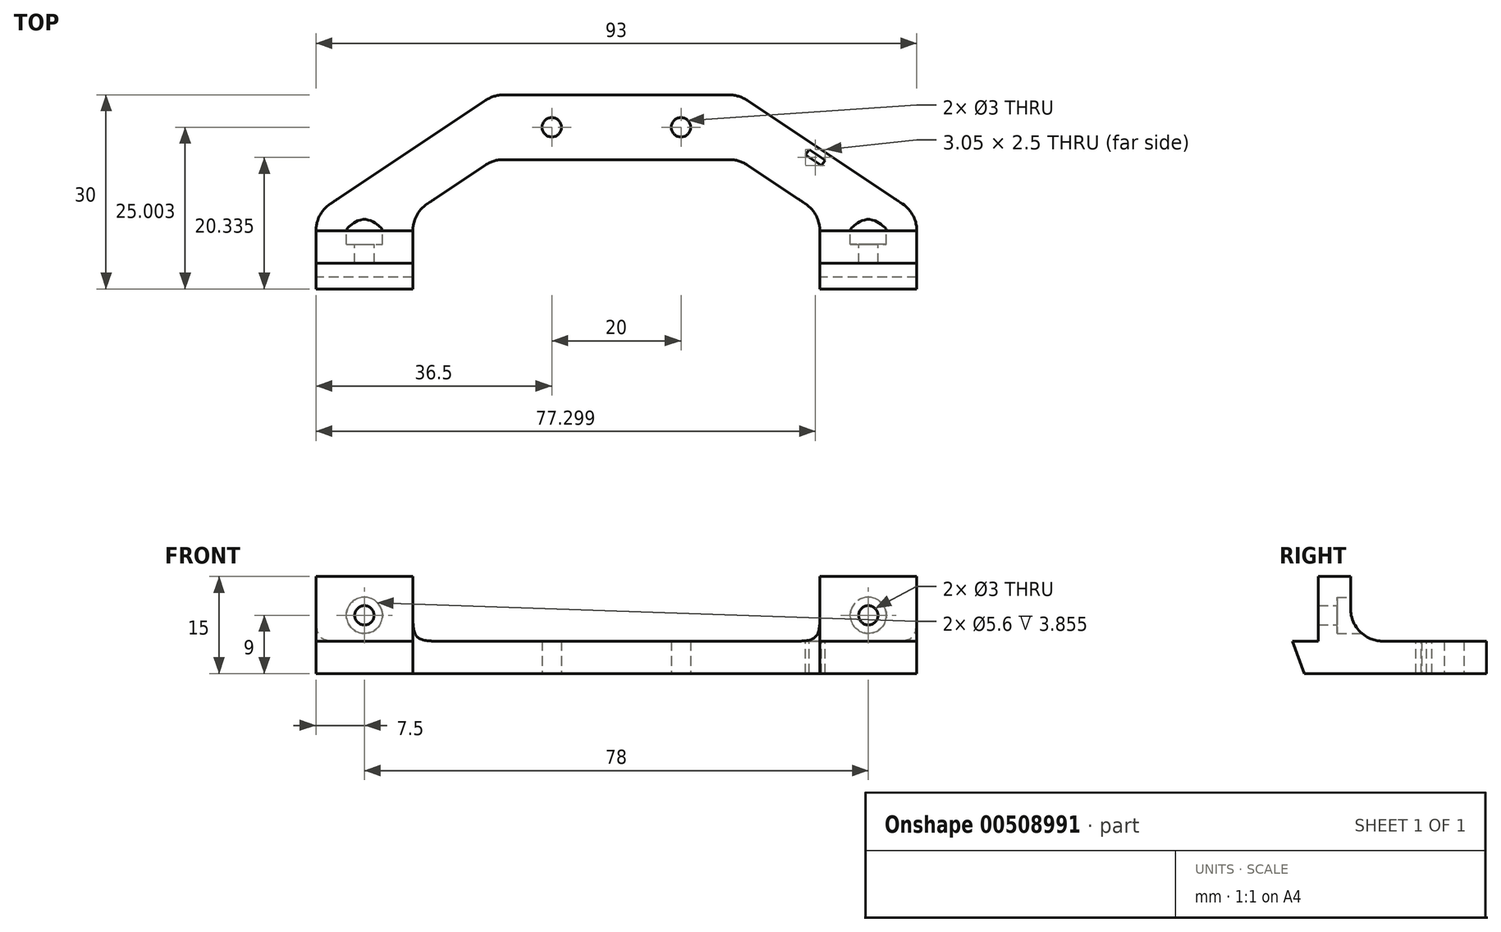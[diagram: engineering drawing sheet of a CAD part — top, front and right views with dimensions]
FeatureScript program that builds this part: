
annotation { "Feature Type Name" : "Feature", "Feature Type Description" : "" }
export const myFeature = defineFeature(function(context is Context, id is Id, definition is map)
    precondition{}
    {
        {
            var Q0;
            Q0=qCreatedBy(makeId("Top.planeOp"),FACE);
            var sketch = newSketch(context, id + "F0", { "sketchPlane" : qUnion([Q0])});
            skLineSegment(sketch, "E0", {"start": v(-65.5, 0) * mm, "end": v(-65.5, 9.07) * mm});
            skLineSegment(sketch, "E1", {"start": v(-63.27, 13.23) * mm, "end": v(-39.26, 29.24) * mm});
            skLineSegment(sketch, "E2", {"start": v(-36.49, 30.08) * mm, "end": v(-1.51, 30.08) * mm});
            skLineSegment(sketch, "E3", {"start": v(1.26, 29.24) * mm, "end": v(25.27, 13.23) * mm});
            skLineSegment(sketch, "E4", {"start": v(27.5, 9.07) * mm, "end": v(27.5, 0) * mm});
            skLineSegment(sketch, "E5", {"start": v(27.5, 0) * mm, "end": v(12.5, 0) * mm});
            skLineSegment(sketch, "E6", {"start": v(12.5, 0) * mm, "end": v(12.5, 9.07) * mm});
            skLineSegment(sketch, "E7", {"start": v(10.27, 13.23) * mm, "end": v(1.26, 19.24) * mm});
            skLineSegment(sketch, "E8", {"start": v(-1.51, 20.08) * mm, "end": v(-36.49, 20.08) * mm});
            skLineSegment(sketch, "E9", {"start": v(-39.26, 19.24) * mm, "end": v(-48.27, 13.23) * mm});
            skLineSegment(sketch, "E10", {"start": v(-50.5, 9.07) * mm, "end": v(-50.5, 0) * mm});
            skLineSegment(sketch, "E11", {"start": v(-50.5, 0) * mm, "end": v(-65.5, 0) * mm});
            skPoint(sketch, "E12.visualSharp", {"position": v(-65.5, 11.75) * mm});
            skArc(sketch, "E12.filletArc", {"start": v(-63.27, 13.23) * mm, "mid": v(-64.9, 11.43) * mm, "end": v(-65.5, 9.07) * mm});
            skPoint(sketch, "E13.visualSharp", {"position": v(-38, 30.08) * mm});
            skArc(sketch, "E13.filletArc", {"start": v(-36.49, 30.08) * mm, "mid": v(-37.94, 29.87) * mm, "end": v(-39.26, 29.24) * mm});
            skPoint(sketch, "E14.visualSharp", {"position": v(0, 30.08) * mm});
            skArc(sketch, "E14.filletArc", {"start": v(1.26, 29.24) * mm, "mid": v(-0.06, 29.87) * mm, "end": v(-1.51, 30.08) * mm});
            skPoint(sketch, "E15.visualSharp", {"position": v(0, 20.08) * mm});
            skArc(sketch, "E15.filletArc", {"start": v(1.26, 19.24) * mm, "mid": v(-0.06, 19.87) * mm, "end": v(-1.51, 20.08) * mm});
            skPoint(sketch, "E16.visualSharp", {"position": v(12.5, 11.75) * mm});
            skArc(sketch, "E16.filletArc", {"start": v(12.5, 9.07) * mm, "mid": v(11.9, 11.43) * mm, "end": v(10.27, 13.23) * mm});
            skPoint(sketch, "E17.visualSharp", {"position": v(27.5, 11.75) * mm});
            skArc(sketch, "E17.filletArc", {"start": v(27.5, 9.07) * mm, "mid": v(26.9, 11.43) * mm, "end": v(25.27, 13.23) * mm});
            skPoint(sketch, "E18.visualSharp", {"position": v(-50.5, 11.75) * mm});
            skArc(sketch, "E18.filletArc", {"start": v(-48.27, 13.23) * mm, "mid": v(-49.9, 11.43) * mm, "end": v(-50.5, 9.07) * mm});
            skPoint(sketch, "E19.visualSharp", {"position": v(-38, 20.08) * mm});
            skArc(sketch, "E19.filletArc", {"start": v(-36.49, 20.08) * mm, "mid": v(-37.94, 19.87) * mm, "end": v(-39.26, 19.24) * mm});
            skPoint(sketch, "E20", {"position": v(-29, 25.08) * mm});
            skPoint(sketch, "E21", {"position": v(-9, 25.08) * mm});
            skLineSegment(sketch, "E22", {"start": v(0, 30.08) * mm, "end": v(0, 20.08) * mm, "construction": true});
            skLineSegment(sketch, "E23", {"start": v(-38, 30.08) * mm, "end": v(-38, 20.08) * mm, "construction": true});
            skSolve(sketch);
        }
        {
            var Q0;
            Q0=makeQuery(id+"F0.imprint","IMPRINT",FACE,{"disambiguationData":[TD([[makeQuery(id+"F0.imprint","IMPRINT",EDGE,{"derivedFrom":sQuery(id+"F0.wireOp",EDGE,"E0")}),-1.0]])]});
            extrude(context, id + "F1", {"entities" : qUnion([Q0]), "depth" : 5 * mm, "offsetDistance" : 25 * mm});
        }
        {
            var Q0;
            Q0=makeQuery(id+"F1.opExtrude","CAP_FACE",FACE,{"disambiguationData":[OSD([sQuery(id+"F0.wireOp",EDGE,"E0"),sQuery(id+"F0.wireOp",EDGE,"E1"),sQuery(id+"F0.wireOp",EDGE,"E2"),sQuery(id+"F0.wireOp",EDGE,"E3"),sQuery(id+"F0.wireOp",EDGE,"E4"),sQuery(id+"F0.wireOp",EDGE,"E5"),sQuery(id+"F0.wireOp",EDGE,"E6"),sQuery(id+"F0.wireOp",EDGE,"E7"),sQuery(id+"F0.wireOp",EDGE,"E8"),sQuery(id+"F0.wireOp",EDGE,"E9"),sQuery(id+"F0.wireOp",EDGE,"E10"),sQuery(id+"F0.wireOp",EDGE,"E11"),sQuery(id+"F0.wireOp",EDGE,"E12.filletArc"),sQuery(id+"F0.wireOp",EDGE,"E13.filletArc"),sQuery(id+"F0.wireOp",EDGE,"E14.filletArc"),sQuery(id+"F0.wireOp",EDGE,"E15.filletArc"),sQuery(id+"F0.wireOp",EDGE,"E16.filletArc"),sQuery(id+"F0.wireOp",EDGE,"E17.filletArc"),sQuery(id+"F0.wireOp",EDGE,"E18.filletArc"),sQuery(id+"F0.wireOp",EDGE,"E19.filletArc")])],"isStart":false});
            var sketch = newSketch(context, id + "F2", { "sketchPlane" : qUnion([Q0])});
            skLineSegment(sketch, "E24.0", {"start": v(-50.5, 0) * mm, "end": v(-65.5, 0) * mm});
            skLineSegment(sketch, "E25.0", {"start": v(-65.5, 0) * mm, "end": v(-65.5, 9.07) * mm});
            skLineSegment(sketch, "E26.0", {"start": v(-50.5, 9.07) * mm, "end": v(-50.5, 0) * mm});
            skLineSegment(sketch, "E27", {"start": v(-65.5, 9.07) * mm, "end": v(-50.5, 9.07) * mm});
            skLineSegment(sketch, "E28.0", {"start": v(27.5, 9.07) * mm, "end": v(27.5, 0) * mm});
            skLineSegment(sketch, "E29.0", {"start": v(27.5, 0) * mm, "end": v(12.5, 0) * mm});
            skLineSegment(sketch, "E30.1", {"start": v(12.5, 0) * mm, "end": v(12.5, 9.07) * mm});
            skLineSegment(sketch, "E31", {"start": v(12.5, 9.07) * mm, "end": v(27.5, 9.07) * mm});
            skLineSegment(sketch, "E32.0", {"start": v(-38, 30.08) * mm, "end": v(-38, 20.08) * mm, "construction": true});
            skLineSegment(sketch, "E33.0", {"start": v(0, 30.08) * mm, "end": v(0, 20.08) * mm, "construction": true});
            skPoint(sketch, "E34", {"position": v(-29, 18.43) * mm});
            skPoint(sketch, "E35", {"position": v(-9, 25.08) * mm});
            skLineSegment(sketch, "E36.0", {"start": v(-36.49, 30.08) * mm, "end": v(-1.51, 30.08) * mm});
            skLineSegment(sketch, "E37.0", {"start": v(-1.51, 20.08) * mm, "end": v(-36.49, 20.08) * mm});
            skLineSegment(sketch, "E38", {"start": v(-65.5, 4.07) * mm, "end": v(-50.5, 4.07) * mm});
            skLineSegment(sketch, "E39", {"start": v(12.5, 4.07) * mm, "end": v(27.5, 4.07) * mm});
            skLineSegment(sketch, "E40.0", {"start": v(1.26, 29.24) * mm, "end": v(25.27, 13.23) * mm});
            skLineSegment(sketch, "E41", {"start": v(10.83, 21.66) * mm, "end": v(13.32, 20) * mm});
            skLineSegment(sketch, "E42", {"start": v(13.32, 20) * mm, "end": v(12.77, 19.17) * mm});
            skLineSegment(sketch, "E43", {"start": v(12.77, 19.17) * mm, "end": v(10.27, 20.83) * mm});
            skLineSegment(sketch, "E44", {"start": v(10.27, 20.83) * mm, "end": v(10.83, 21.66) * mm});
            skSolve(sketch);
        }
        {
            var Q0;
            {var subQ0=sQuery(id+"F2.wireOp",EDGE,"E27");Q0=makeQuery(id+"F2.imprint","IMPRINT",FACE,{"disambiguationData":[TD([[makeQuery(id+"F2.imprint","IMPRINT",EDGE,{"derivedFrom":subQ0}),-1.0]])]});}
            var Q1;
            {var subQ0=sQuery(id+"F2.wireOp",EDGE,"E31");Q1=makeQuery(id+"F2.imprint","IMPRINT",FACE,{"disambiguationData":[TD([[makeQuery(id+"F2.imprint","IMPRINT",EDGE,{"derivedFrom":subQ0}),-1.0]])]});}
            extrude(context, id + "F3", {"entities" : qUnion([Q0, Q1]), "operationType" : NewBodyOperationType.ADD, "depth" : 10 * mm, "offsetDistance" : 25 * mm});
        }
        {
            var Q0;
            Q0=makeQuery(id+"F3.opExtrude","SWEPT_FACE",FACE,{"disambiguationData":[OSD([sQuery(id+"F2.wireOp",EDGE,"E27")])]});
            var sketch = newSketch(context, id + "F4", { "sketchPlane" : qUnion([Q0])});
            skPoint(sketch, "E45", {"position": v(58, 9) * mm});
            skPoint(sketch, "E45.positionSnap0", {"position": v(58, 5) * mm});
            skSolve(sketch);
        }
        {
            var Q0;
            Q0=makeQuery(id+"F3.opExtrude","SWEPT_FACE",FACE,{"disambiguationData":[OSD([sQuery(id+"F2.wireOp",EDGE,"E31")])]});
            var sketch = newSketch(context, id + "F5", { "sketchPlane" : qUnion([Q0])});
            skPoint(sketch, "E46", {"position": v(-20, 9) * mm});
            skPoint(sketch, "E46.positionSnap0", {"position": v(-20, 5) * mm});
            skSolve(sketch);
        }
        {
            var Q0;
            Q0=sQuery(id+"F4.wireOp",VERTEX,"E45");
            var Q1;
            Q1=sQuery(id+"F5.wireOp",VERTEX,"E46");
            var Q2;
            Q2=makeQuery(id+"F1.opExtrude","SWEPT_BODY",BODY,{"disambiguationData":[OSD([sQuery(id+"F0.wireOp",EDGE,"E0"),sQuery(id+"F0.wireOp",EDGE,"E1"),sQuery(id+"F0.wireOp",EDGE,"E2"),sQuery(id+"F0.wireOp",EDGE,"E3"),sQuery(id+"F0.wireOp",EDGE,"E4"),sQuery(id+"F0.wireOp",EDGE,"E5"),sQuery(id+"F0.wireOp",EDGE,"E6"),sQuery(id+"F0.wireOp",EDGE,"E7"),sQuery(id+"F0.wireOp",EDGE,"E8"),sQuery(id+"F0.wireOp",EDGE,"E9"),sQuery(id+"F0.wireOp",EDGE,"E10"),sQuery(id+"F0.wireOp",EDGE,"E11"),sQuery(id+"F0.wireOp",EDGE,"E12.filletArc"),sQuery(id+"F0.wireOp",EDGE,"E13.filletArc"),sQuery(id+"F0.wireOp",EDGE,"E14.filletArc"),sQuery(id+"F0.wireOp",EDGE,"E15.filletArc"),sQuery(id+"F0.wireOp",EDGE,"E16.filletArc"),sQuery(id+"F0.wireOp",EDGE,"E17.filletArc"),sQuery(id+"F0.wireOp",EDGE,"E18.filletArc"),sQuery(id+"F0.wireOp",EDGE,"E19.filletArc")])]});
            hole(context, id + "F6", {"style" : HoleStyle.C_BORE, "endStyle" : HoleEndStyle.THROUGH, "holeDiameter" : 3 * mm, "cBoreDiameter" : 5.6 * mm, "cBoreDepth" : 2.1 * mm, "isTappedThrough" : true, "tappedDepth" : 12 * mm, "tapClearance" : 3, "startFromSketch" : true, "locations" : qUnion([Q0, Q1]), "scope" : qUnion([Q2])});
        }
        {
            var Q0;
            Q0=sQuery(id+"F0.wireOp",VERTEX,"E20");
            var Q1;
            Q1=sQuery(id+"F0.wireOp",VERTEX,"E21");
            var Q2;
            Q2=makeQuery(id+"F1.opExtrude","SWEPT_BODY",BODY,{"disambiguationData":[OSD([sQuery(id+"F0.wireOp",EDGE,"E0"),sQuery(id+"F0.wireOp",EDGE,"E1"),sQuery(id+"F0.wireOp",EDGE,"E2"),sQuery(id+"F0.wireOp",EDGE,"E3"),sQuery(id+"F0.wireOp",EDGE,"E4"),sQuery(id+"F0.wireOp",EDGE,"E5"),sQuery(id+"F0.wireOp",EDGE,"E6"),sQuery(id+"F0.wireOp",EDGE,"E7"),sQuery(id+"F0.wireOp",EDGE,"E8"),sQuery(id+"F0.wireOp",EDGE,"E9"),sQuery(id+"F0.wireOp",EDGE,"E10"),sQuery(id+"F0.wireOp",EDGE,"E11"),sQuery(id+"F0.wireOp",EDGE,"E12.filletArc"),sQuery(id+"F0.wireOp",EDGE,"E13.filletArc"),sQuery(id+"F0.wireOp",EDGE,"E14.filletArc"),sQuery(id+"F0.wireOp",EDGE,"E15.filletArc"),sQuery(id+"F0.wireOp",EDGE,"E16.filletArc"),sQuery(id+"F0.wireOp",EDGE,"E17.filletArc"),sQuery(id+"F0.wireOp",EDGE,"E18.filletArc"),sQuery(id+"F0.wireOp",EDGE,"E19.filletArc")])]});
            hole(context, id + "F7", {"style" : HoleStyle.SIMPLE, "endStyle" : HoleEndStyle.THROUGH, "oppositeDirection" : true, "holeDiameter" : 3 * mm, "isTappedThrough" : true, "tappedDepth" : 12 * mm, "tapClearance" : 3, "startFromSketch" : true, "locations" : qUnion([Q0, Q1]), "scope" : qUnion([Q2])});
        }
        {
            var Q0;
            Q0=makeQuery(id+"F3.opExtrude","CAP_EDGE",EDGE,{"disambiguationData":[OSD([sQuery(id+"F2.wireOp",EDGE,"E31")])],"isStart":true});
            var Q1;
            Q1=makeQuery(id+"F3.opExtrude","CAP_EDGE",EDGE,{"disambiguationData":[OSD([sQuery(id+"F2.wireOp",EDGE,"E27")])],"isStart":true});
            fillet(context, id + "F8", {"entities" : qUnion([Q0, Q1]), "radius" : 5 * mm, "tangentPropagation" : true, "allowEdgeOverflow" : false});
        }
        {
            var Q0;
            Q0=makeQuery(id+"F1.opExtrude","CAP_EDGE",EDGE,{"disambiguationData":[OSD([sQuery(id+"F0.wireOp",EDGE,"E5")])],"isStart":true});
            var Q1;
            Q1=makeQuery(id+"F1.opExtrude","CAP_EDGE",EDGE,{"disambiguationData":[OSD([sQuery(id+"F0.wireOp",EDGE,"E11")])],"isStart":true});
            chamfer(context, id + "F9", {"entities" : qUnion([Q0, Q1]), "chamferType" : ChamferType.OFFSET_ANGLE, "width" : 1.9 * mm, "oppositeDirection" : false, "angle" : 70 * degree, "tangentPropagation" : true});
        }
        {
            var Q0;
            Q0=makeQuery(id+"F2.imprint","IMPRINT",FACE,{"disambiguationData":[TD([[makeQuery(id+"F2.imprint","IMPRINT",EDGE,{"derivedFrom":sQuery(id+"F2.wireOp",EDGE,"E41")}),-1.0]])]});
            extrude(context, id + "F10", {"entities" : qUnion([Q0]), "operationType" : NewBodyOperationType.ADD, "depth" : 25 * mm, "offsetDistance" : 25 * mm});
        }
        {
            var Q0;
            Q0=makeQuery(id+"F10.opExtrude","CAP_FACE",FACE,{"disambiguationData":[OSD([sQuery(id+"F2.wireOp",EDGE,"E41"),sQuery(id+"F2.wireOp",EDGE,"E42"),sQuery(id+"F2.wireOp",EDGE,"E43"),sQuery(id+"F2.wireOp",EDGE,"E44")])],"isStart":false});
            extrude(context, id + "F11", {"entities" : qUnion([Q0]), "operationType" : NewBodyOperationType.REMOVE, "endBound" : BoundingType.THROUGH_ALL, "oppositeDirection" : true, "depth" : 25 * mm, "offsetDistance" : 25 * mm});
        }
    });
